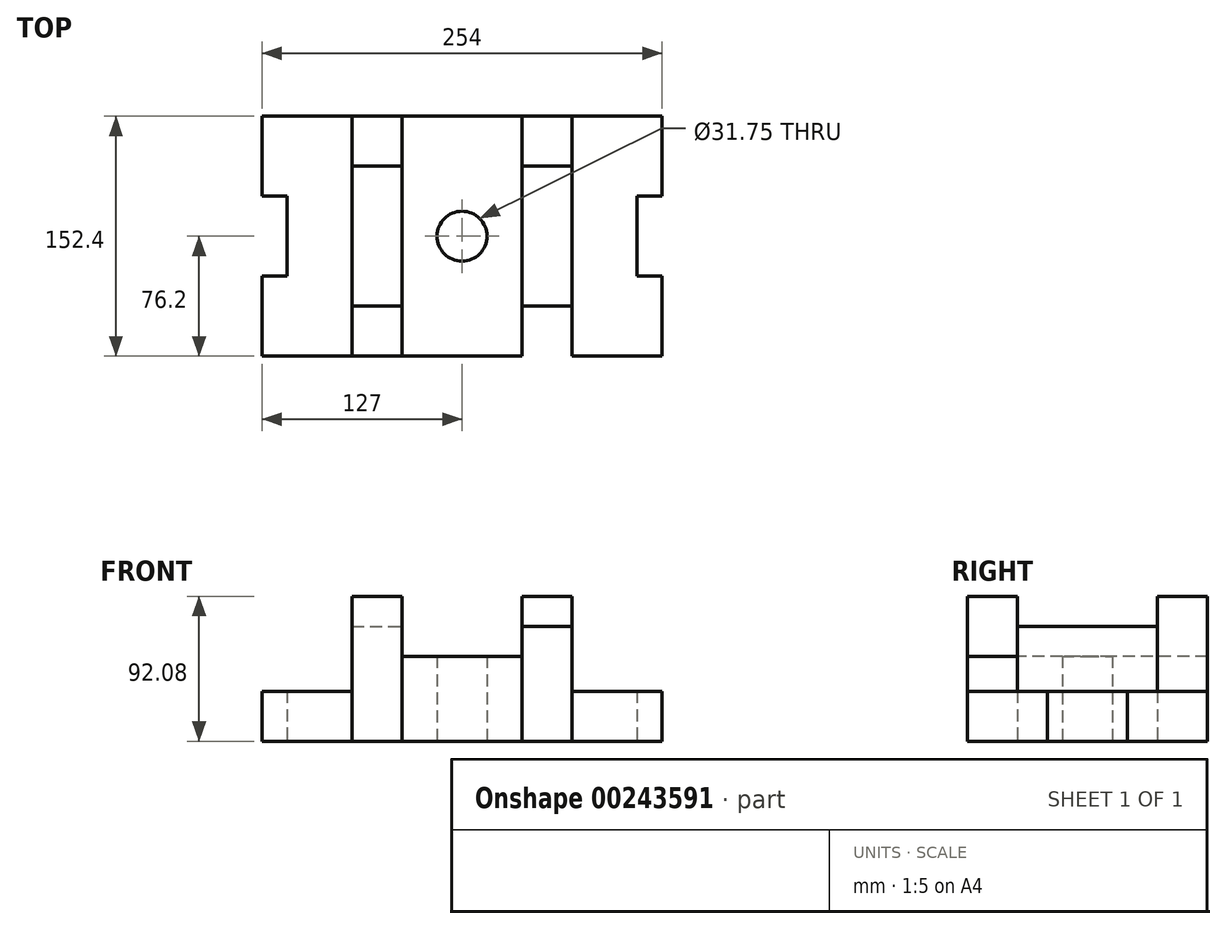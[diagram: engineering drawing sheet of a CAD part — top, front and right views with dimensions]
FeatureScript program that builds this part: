
annotation { "Feature Type Name" : "Feature", "Feature Type Description" : "" }
export const myFeature = defineFeature(function(context is Context, id is Id, definition is map)
    precondition{}
    {
        {
            var Q0;
            Q0=qCreatedBy(makeId("Top.planeOp"),FACE);
            var sketch = newSketch(context, id + "F0", { "sketchPlane" : qUnion([Q0])});
            skCircle(sketch, "E0", {"center": v(0, 0) * mm, "radius": 15.88 * mm});
            skLineSegment(sketch, "E1", {"start": v(0, -76.2) * mm, "end": v(-127, -76.2) * mm});
            skLineSegment(sketch, "E2", {"start": v(-127, -25.4) * mm, "end": v(-111.13, -25.4) * mm});
            skLineSegment(sketch, "E3", {"start": v(-111.13, -25.4) * mm, "end": v(-111.13, 25.4) * mm});
            skLineSegment(sketch, "E4", {"start": v(-127, -25.4) * mm, "end": v(-127, -76.2) * mm});
            skLineSegment(sketch, "E5", {"start": v(-111.13, 25.4) * mm, "end": v(-127, 25.4) * mm});
            skLineSegment(sketch, "E6", {"start": v(-127, 25.4) * mm, "end": v(-127, 76.2) * mm});
            skLineSegment(sketch, "E7", {"start": v(-127, 76.2) * mm, "end": v(0, 76.2) * mm});
            skLineSegment(sketch, "E8.MirrorCS", {"start": v(0, -76.2) * mm, "end": v(127, -76.2) * mm});
            skLineSegment(sketch, "E9.MirrorCS", {"start": v(127, -25.4) * mm, "end": v(127, -76.2) * mm});
            skLineSegment(sketch, "E10.MirrorCS", {"start": v(127, -25.4) * mm, "end": v(111.13, -25.4) * mm});
            skLineSegment(sketch, "E11.MirrorCS", {"start": v(111.13, -25.4) * mm, "end": v(111.13, 25.4) * mm});
            skLineSegment(sketch, "E12.MirrorCS", {"start": v(111.13, 25.4) * mm, "end": v(127, 25.4) * mm});
            skLineSegment(sketch, "E13.MirrorCS", {"start": v(127, 25.4) * mm, "end": v(127, 76.2) * mm});
            skLineSegment(sketch, "E14.MirrorCS", {"start": v(127, 76.2) * mm, "end": v(0, 76.2) * mm});
            skLineSegment(sketch, "E15", {"start": v(69.85, 44.46) * mm, "end": v(69.85, 76.2) * mm});
            skLineSegment(sketch, "E16", {"start": v(69.85, 44.46) * mm, "end": v(38.1, 44.46) * mm});
            skLineSegment(sketch, "E17", {"start": v(38.1, 44.46) * mm, "end": v(38.1, 76.2) * mm});
            skLineSegment(sketch, "E18", {"start": v(38.1, 76.2) * mm, "end": v(38.1, -76.2) * mm});
            skLineSegment(sketch, "E19", {"start": v(38.1, -76.2) * mm, "end": v(69.85, -76.2) * mm});
            skLineSegment(sketch, "E20", {"start": v(69.85, -76.2) * mm, "end": v(69.85, 44.46) * mm});
            skLineSegment(sketch, "E21.MirrorCS", {"start": v(69.85, -44.46) * mm, "end": v(38.1, -44.46) * mm});
            skPoint(sketch, "E22.start.orphan", {"position": v(38.1, 0) * mm});
            skLineSegment(sketch, "E23.MirrorCS", {"start": v(-38.1, 76.2) * mm, "end": v(-38.1, -76.2) * mm});
            skLineSegment(sketch, "E24.MirrorCS", {"start": v(-69.85, 44.46) * mm, "end": v(-38.1, 44.46) * mm});
            skLineSegment(sketch, "E25.MirrorCS", {"start": v(-69.85, 44.46) * mm, "end": v(-69.85, 76.2) * mm});
            skLineSegment(sketch, "E26.MirrorCS", {"start": v(-69.85, -76.2) * mm, "end": v(-69.85, 44.46) * mm});
            skLineSegment(sketch, "E27.MirrorCS", {"start": v(-69.85, -44.46) * mm, "end": v(-38.1, -44.46) * mm});
            skSolve(sketch);
        }
        {
            var Q0;
            Q0=makeQuery(id+"F0.imprint","IMPRINT",FACE,{"disambiguationData":[TD([[makeQuery(id+"F0.imprint","IMPRINT",EDGE,{"derivedFrom":sQuery(id+"F0.wireOp",EDGE,"E2")}),-1.0]])]});
            var Q1;
            {var subQ0=sQuery(id+"F0.wireOp",EDGE,"E9.MirrorCS");Q1=makeQuery(id+"F0.imprint","IMPRINT",FACE,{"disambiguationData":[TD([[makeQuery(id+"F0.imprint","IMPRINT",EDGE,{"derivedFrom":subQ0}),-1.0]])]});}
            extrude(context, id + "F1", {"entities" : qUnion([Q0, Q1]), "depth" : 31.75 * mm});
        }
        {
            var Q0;
            Q0=makeQuery(id+"F0.imprint","IMPRINT",FACE,{"disambiguationData":[TD([[makeQuery(id+"F0.imprint","IMPRINT",EDGE,{"derivedFrom":sQuery(id+"F0.wireOp",EDGE,"E0")}),-1.0]])]});
            extrude(context, id + "F2", {"entities" : qUnion([Q0]), "depth" : 53.97 * mm});
        }
        {
            var Q0;
            {var subQ0=sQuery(id+"F0.wireOp",EDGE,"E24.MirrorCS");Q0=makeQuery(id+"F0.imprint","IMPRINT",FACE,{"disambiguationData":[TD([[makeQuery(id+"F0.imprint","IMPRINT",EDGE,{"derivedFrom":subQ0}),-1.0]])]});}
            var Q1;
            {var subQ0=sQuery(id+"F0.wireOp",EDGE,"E16");Q1=makeQuery(id+"F0.imprint","IMPRINT",FACE,{"disambiguationData":[TD([[makeQuery(id+"F0.imprint","IMPRINT",EDGE,{"derivedFrom":subQ0}),1.0]])]});}
            extrude(context, id + "F3", {"entities" : qUnion([Q0, Q1]), "depth" : 73.02 * mm});
        }
        {
            var Q0;
            {var subQ4=sQuery(id+"F0.wireOp",EDGE,"E24.MirrorCS");Q0=makeQuery(id+"F0.imprint","IMPRINT",FACE,{"disambiguationData":[TD([[makeQuery(id+"F0.imprint","IMPRINT",EDGE,{"derivedFrom":subQ4}),1.0]])]});}
            var Q1;
            {var subQ5=sQuery(id+"F0.wireOp",EDGE,"E27.MirrorCS");Q1=makeQuery(id+"F0.imprint","IMPRINT",FACE,{"disambiguationData":[TD([[makeQuery(id+"F0.imprint","IMPRINT",EDGE,{"derivedFrom":subQ5}),-1.0]])]});}
            var Q2;
            {var subQ0=sQuery(id+"F0.wireOp",EDGE,"E19");Q2=makeQuery(id+"F0.imprint","IMPRINT",FACE,{"disambiguationData":[TD([[makeQuery(id+"F0.imprint","IMPRINT",EDGE,{"derivedFrom":subQ0}),1.0]])]});}
            var Q3;
            {var subQ0=sQuery(id+"F0.wireOp",EDGE,"E15");Q3=makeQuery(id+"F0.imprint","IMPRINT",FACE,{"disambiguationData":[TD([[makeQuery(id+"F0.imprint","IMPRINT",EDGE,{"derivedFrom":subQ0}),1.0]])]});}
            extrude(context, id + "F4", {"entities" : qUnion([Q0, Q1, Q2, Q3]), "depth" : 92.07 * mm});
        }
    });
